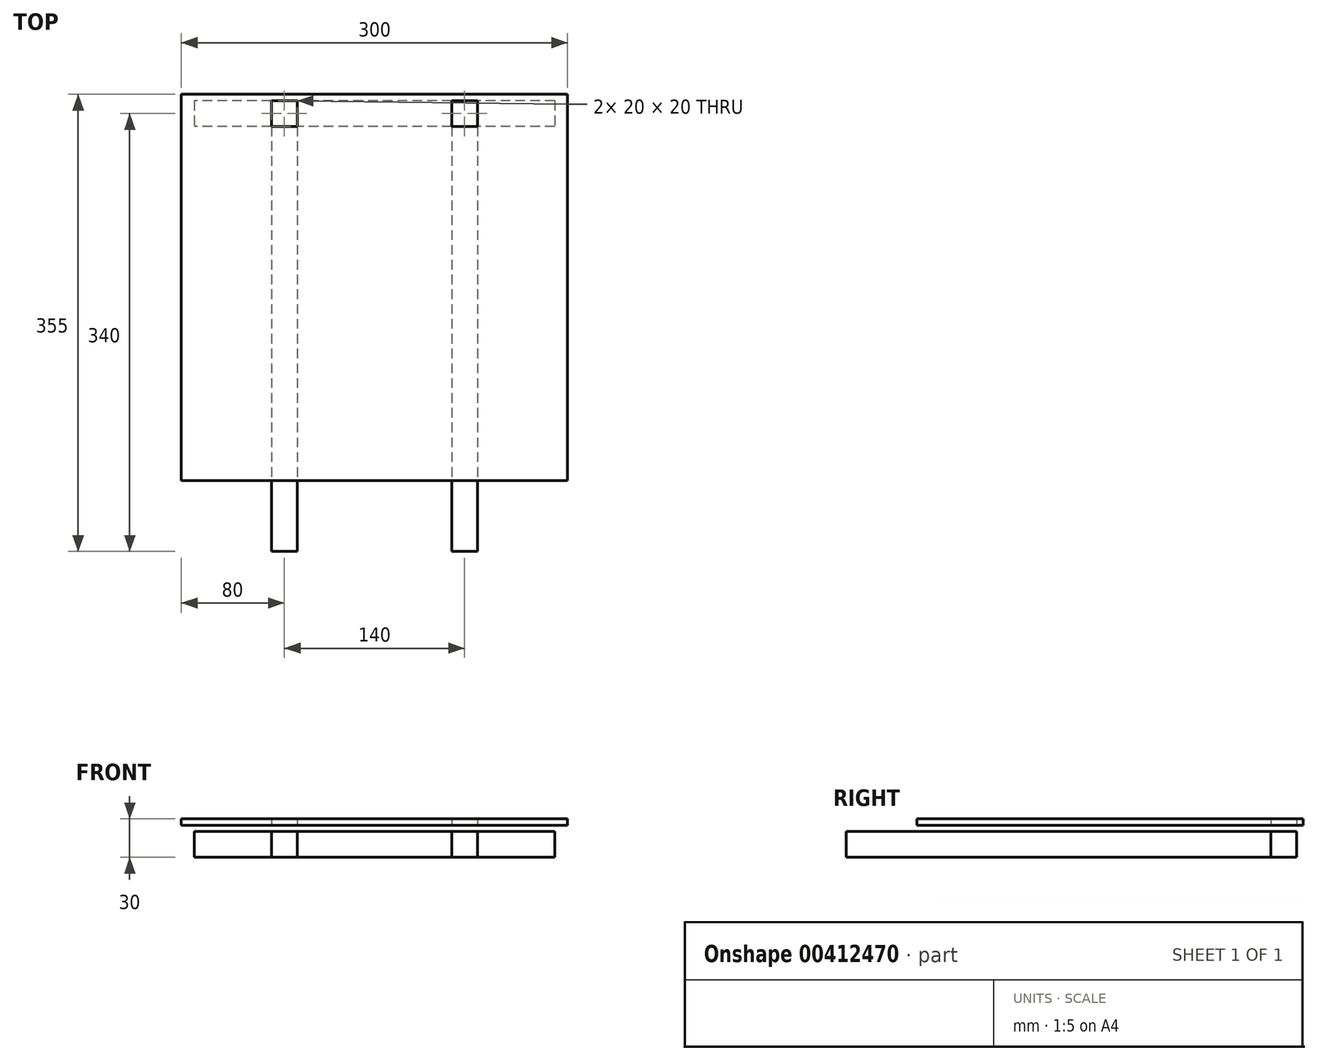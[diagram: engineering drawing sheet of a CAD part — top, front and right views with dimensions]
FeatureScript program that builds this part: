
annotation { "Feature Type Name" : "Feature", "Feature Type Description" : "" }
export const myFeature = defineFeature(function(context is Context, id is Id, definition is map)
    precondition{}
    {
        {
            var Q0;
            Q0=qCreatedBy(makeId("Top.planeOp"),FACE);
            var sketch = newSketch(context, id + "F0", { "sketchPlane" : qUnion([Q0])});
            skLineSegment(sketch, "E0.bottom", {"start": v(150, 150) * mm, "end": v(-150, 150) * mm});
            skLineSegment(sketch, "E0.top", {"start": v(150, -150) * mm, "end": v(-150, -150) * mm});
            skLineSegment(sketch, "E0.left", {"start": v(150, 150) * mm, "end": v(150, -150) * mm});
            skLineSegment(sketch, "E0.right", {"start": v(-150, 150) * mm, "end": v(-150, -150) * mm});
            skPoint(sketch, "E0.middle", {"position": v(0, 0) * mm});
            skPoint(sketch, "E1", {"position": v(0, 135) * mm});
            skLineSegment(sketch, "E2.bottom", {"start": v(140, 145) * mm, "end": v(-140, 145) * mm});
            skLineSegment(sketch, "E2.top", {"start": v(140, 125) * mm, "end": v(-140, 125) * mm});
            skLineSegment(sketch, "E2.left", {"start": v(140, 145) * mm, "end": v(140, 125) * mm});
            skLineSegment(sketch, "E2.right", {"start": v(-140, 145) * mm, "end": v(-140, 125) * mm});
            skLineSegment(sketch, "E3.bottom", {"start": v(-80, 145) * mm, "end": v(-60, 145) * mm});
            skLineSegment(sketch, "E3.top", {"start": v(-80, -205) * mm, "end": v(-60, -205) * mm});
            skLineSegment(sketch, "E3.left", {"start": v(-80, 145) * mm, "end": v(-80, -205) * mm});
            skLineSegment(sketch, "E3.right", {"start": v(-60, 145) * mm, "end": v(-60, -205) * mm});
            skLineSegment(sketch, "E4.MirrorCS", {"start": v(80, 145) * mm, "end": v(60, 145) * mm});
            skLineSegment(sketch, "E5.MirrorCS", {"start": v(80, 145) * mm, "end": v(80, -205) * mm});
            skLineSegment(sketch, "E6.MirrorCS", {"start": v(60, 145) * mm, "end": v(60, -205) * mm});
            skLineSegment(sketch, "E7.MirrorCS", {"start": v(80, -205) * mm, "end": v(60, -205) * mm});
            skSolve(sketch);
        }
        {
            var Q0;
            {var subQ0=sQuery(id+"F0.wireOp",EDGE,"E2.right");var subQ1=sQuery(id+"F0.wireOp",EDGE,"E0.bottom");var subQ2=makeQuery(id+"F0.imprint","INTERSECT",VERTEX,{"derivedFrom":[subQ1,subQ0]});Q0=makeQuery(id+"F0.imprint","IMPRINT",FACE,{"disambiguationData":[TD([[makeQuery(id+"F0.imprint","IMPRINT",EDGE,{"disambiguationData":[TD([[subQ2,1.0]])],"derivedFrom":subQ1}),1.0]])]});}
            var Q1;
            {var subQ0=sQuery(id+"F0.wireOp",EDGE,"E0.right");Q1=makeQuery(id+"F0.imprint","IMPRINT",FACE,{"disambiguationData":[TD([[makeQuery(id+"F0.imprint","IMPRINT",EDGE,{"derivedFrom":subQ0}),1.0]])]});}
            var Q2;
            {var subQ0=sQuery(id+"F0.wireOp",EDGE,"E3.right");var subQ1=sQuery(id+"F0.wireOp",EDGE,"E0.top");var subQ2=makeQuery(id+"F0.imprint","INTERSECT",VERTEX,{"derivedFrom":[subQ1,subQ0]});Q2=makeQuery(id+"F0.imprint","IMPRINT",FACE,{"disambiguationData":[TD([[makeQuery(id+"F0.imprint","IMPRINT",EDGE,{"disambiguationData":[TD([[subQ2,-1.0]])],"derivedFrom":subQ1}),-1.0]])]});}
            var Q3;
            {var subQ0=sQuery(id+"F0.wireOp",EDGE,"E6.MirrorCS");var subQ1=sQuery(id+"F0.wireOp",EDGE,"E0.top");var subQ2=makeQuery(id+"F0.imprint","INTERSECT",VERTEX,{"derivedFrom":[subQ1,subQ0]});Q3=makeQuery(id+"F0.imprint","IMPRINT",FACE,{"disambiguationData":[TD([[makeQuery(id+"F0.imprint","IMPRINT",EDGE,{"disambiguationData":[TD([[subQ2,-1.0]])],"derivedFrom":subQ1}),-1.0]])]});}
            var Q4;
            {var subQ0=sQuery(id+"F0.wireOp",EDGE,"E5.MirrorCS");var subQ1=sQuery(id+"F0.wireOp",EDGE,"E0.top");var subQ2=makeQuery(id+"F0.imprint","INTERSECT",VERTEX,{"derivedFrom":[subQ1,subQ0]});Q4=makeQuery(id+"F0.imprint","IMPRINT",FACE,{"disambiguationData":[TD([[makeQuery(id+"F0.imprint","IMPRINT",EDGE,{"disambiguationData":[TD([[subQ2,-1.0]])],"derivedFrom":subQ1}),-1.0]])]});}
            var Q5;
            {var subQ0=sQuery(id+"F0.wireOp",EDGE,"E0.left");Q5=makeQuery(id+"F0.imprint","IMPRINT",FACE,{"disambiguationData":[TD([[makeQuery(id+"F0.imprint","IMPRINT",EDGE,{"derivedFrom":subQ0}),-1.0]])]});}
            var Q6;
            {var subQ0=sQuery(id+"F0.wireOp",EDGE,"E6.MirrorCS");var subQ1=sQuery(id+"F0.wireOp",EDGE,"E0.bottom");var subQ2=makeQuery(id+"F0.imprint","INTERSECT",VERTEX,{"derivedFrom":[subQ1,subQ0]});Q6=makeQuery(id+"F0.imprint","IMPRINT",FACE,{"disambiguationData":[TD([[makeQuery(id+"F0.imprint","IMPRINT",EDGE,{"disambiguationData":[TD([[subQ2,-1.0]])],"derivedFrom":subQ1}),1.0]])]});}
            var Q7;
            {var subQ0=sQuery(id+"F0.wireOp",EDGE,"E2.left");var subQ1=sQuery(id+"F0.wireOp",EDGE,"E0.bottom");var subQ2=makeQuery(id+"F0.imprint","INTERSECT",VERTEX,{"derivedFrom":[subQ1,subQ0]});Q7=makeQuery(id+"F0.imprint","IMPRINT",FACE,{"disambiguationData":[TD([[makeQuery(id+"F0.imprint","IMPRINT",EDGE,{"disambiguationData":[TD([[subQ2,-1.0]])],"derivedFrom":subQ1}),1.0]])]});}
            var Q8;
            {var subQ0=sQuery(id+"F0.wireOp",EDGE,"E2.right");Q8=makeQuery(id+"F0.imprint","IMPRINT",FACE,{"disambiguationData":[TD([[makeQuery(id+"F0.imprint","IMPRINT",EDGE,{"derivedFrom":subQ0}),1.0]])]});}
            var Q9;
            {var subQ5=sQuery(id+"F0.wireOp",EDGE,"E3.bottom");Q9=makeQuery(id+"F0.imprint","IMPRINT",FACE,{"disambiguationData":[TD([[makeQuery(id+"F0.imprint","IMPRINT",EDGE,{"derivedFrom":subQ5}),-1.0]])]});}
            var Q10;
            {var subQ3=sQuery(id+"F0.wireOp",EDGE,"E6.MirrorCS");var subQ5=sQuery(id+"F0.wireOp",EDGE,"E2.top");var subQ6=makeQuery(id+"F0.imprint","INTERSECT",VERTEX,{"derivedFrom":[subQ5,subQ3]});Q10=makeQuery(id+"F0.imprint","IMPRINT",FACE,{"disambiguationData":[TD([[makeQuery(id+"F0.imprint","IMPRINT",EDGE,{"disambiguationData":[TD([[subQ6,-1.0]])],"derivedFrom":subQ5}),-1.0]])]});}
            var Q11;
            {var subQ5=sQuery(id+"F0.wireOp",EDGE,"E4.MirrorCS");Q11=makeQuery(id+"F0.imprint","IMPRINT",FACE,{"disambiguationData":[TD([[makeQuery(id+"F0.imprint","IMPRINT",EDGE,{"derivedFrom":subQ5}),1.0]])]});}
            var Q12;
            {var subQ0=sQuery(id+"F0.wireOp",EDGE,"E2.left");Q12=makeQuery(id+"F0.imprint","IMPRINT",FACE,{"disambiguationData":[TD([[makeQuery(id+"F0.imprint","IMPRINT",EDGE,{"derivedFrom":subQ0}),-1.0]])]});}
            extrude(context, id + "F1", {"entities" : qUnion([Q0, Q1, Q2, Q3, Q4, Q5, Q6, Q7, Q8, Q9, Q10, Q11, Q12]), "depth" : 30 * mm, "hasSecondDirection" : true, "secondDirectionOppositeDirection" : false, "secondDirectionDepth" : 25 * mm});
        }
        {
            var Q0;
            {var subQ0=sQuery(id+"F0.wireOp",EDGE,"E2.right");Q0=makeQuery(id+"F0.imprint","IMPRINT",FACE,{"disambiguationData":[TD([[makeQuery(id+"F0.imprint","IMPRINT",EDGE,{"derivedFrom":subQ0}),1.0]])]});}
            var Q1;
            {var subQ5=sQuery(id+"F0.wireOp",EDGE,"E3.bottom");Q1=makeQuery(id+"F0.imprint","IMPRINT",FACE,{"disambiguationData":[TD([[makeQuery(id+"F0.imprint","IMPRINT",EDGE,{"derivedFrom":subQ5}),-1.0]])]});}
            var Q2;
            {var subQ3=sQuery(id+"F0.wireOp",EDGE,"E6.MirrorCS");var subQ5=sQuery(id+"F0.wireOp",EDGE,"E2.top");var subQ6=makeQuery(id+"F0.imprint","INTERSECT",VERTEX,{"derivedFrom":[subQ5,subQ3]});Q2=makeQuery(id+"F0.imprint","IMPRINT",FACE,{"disambiguationData":[TD([[makeQuery(id+"F0.imprint","IMPRINT",EDGE,{"disambiguationData":[TD([[subQ6,-1.0]])],"derivedFrom":subQ5}),-1.0]])]});}
            var Q3;
            {var subQ5=sQuery(id+"F0.wireOp",EDGE,"E4.MirrorCS");Q3=makeQuery(id+"F0.imprint","IMPRINT",FACE,{"disambiguationData":[TD([[makeQuery(id+"F0.imprint","IMPRINT",EDGE,{"derivedFrom":subQ5}),1.0]])]});}
            var Q4;
            {var subQ4=sQuery(id+"F0.wireOp",EDGE,"E2.left");Q4=makeQuery(id+"F0.imprint","IMPRINT",FACE,{"disambiguationData":[TD([[makeQuery(id+"F0.imprint","IMPRINT",EDGE,{"derivedFrom":subQ4}),-1.0]])]});}
            var Q5;
            {var subQ0=sQuery(id+"F0.wireOp",EDGE,"E5.MirrorCS");var subQ1=sQuery(id+"F0.wireOp",EDGE,"E0.top");var subQ2=makeQuery(id+"F0.imprint","INTERSECT",VERTEX,{"derivedFrom":[subQ1,subQ0]});Q5=makeQuery(id+"F0.imprint","IMPRINT",FACE,{"disambiguationData":[TD([[makeQuery(id+"F0.imprint","IMPRINT",EDGE,{"disambiguationData":[TD([[subQ2,-1.0]])],"derivedFrom":subQ1}),-1.0]])]});}
            var Q6;
            {var subQ0=sQuery(id+"F0.wireOp",EDGE,"E3.right");var subQ1=sQuery(id+"F0.wireOp",EDGE,"E0.top");var subQ2=makeQuery(id+"F0.imprint","INTERSECT",VERTEX,{"derivedFrom":[subQ1,subQ0]});Q6=makeQuery(id+"F0.imprint","IMPRINT",FACE,{"disambiguationData":[TD([[makeQuery(id+"F0.imprint","IMPRINT",EDGE,{"disambiguationData":[TD([[subQ2,-1.0]])],"derivedFrom":subQ1}),-1.0]])]});}
            var Q7;
            {var subQ5=sQuery(id+"F0.wireOp",EDGE,"E3.top");Q7=makeQuery(id+"F0.imprint","IMPRINT",FACE,{"disambiguationData":[TD([[makeQuery(id+"F0.imprint","IMPRINT",EDGE,{"derivedFrom":subQ5}),1.0]])]});}
            var Q8;
            {var subQ5=sQuery(id+"F0.wireOp",EDGE,"E7.MirrorCS");Q8=makeQuery(id+"F0.imprint","IMPRINT",FACE,{"disambiguationData":[TD([[makeQuery(id+"F0.imprint","IMPRINT",EDGE,{"derivedFrom":subQ5}),-1.0]])]});}
            var Q9;
            {var subQ0=sQuery(id+"F0.wireOp",EDGE,"E6.MirrorCS");var subQ1=sQuery(id+"F0.wireOp",EDGE,"E0.bottom");var subQ2=makeQuery(id+"F0.imprint","INTERSECT",VERTEX,{"derivedFrom":[subQ1,subQ0]});Q9=makeQuery(id+"F0.imprint","IMPRINT",FACE,{"disambiguationData":[TD([[makeQuery(id+"F0.imprint","IMPRINT",EDGE,{"disambiguationData":[TD([[subQ2,-1.0]])],"derivedFrom":subQ1}),-1.0]])]});}
            extrude(context, id + "F2", {"entities" : qUnion([Q0, Q1, Q2, Q3, Q4, Q5, Q6, Q7, Q8, Q9]), "depth" : 20 * mm});
        }
    });
